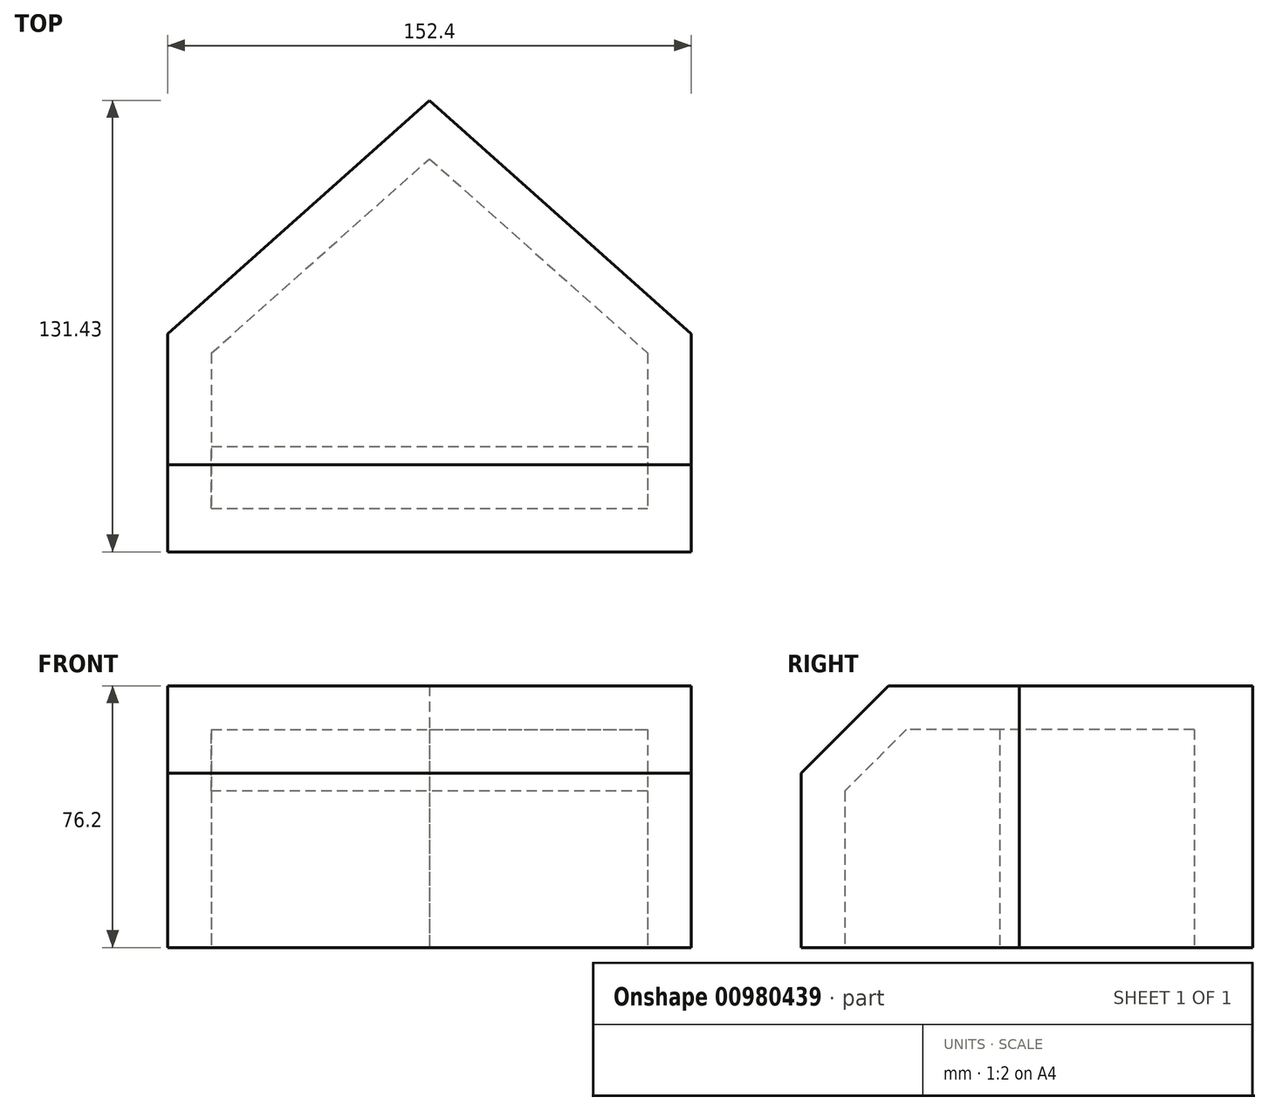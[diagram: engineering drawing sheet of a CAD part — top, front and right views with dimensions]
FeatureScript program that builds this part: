
annotation { "Feature Type Name" : "Feature", "Feature Type Description" : "" }
export const myFeature = defineFeature(function(context is Context, id is Id, definition is map)
    precondition{}
    {
        {
            var Q0;
            Q0=qCreatedBy(makeId("Top.planeOp"),FACE);
            var sketch = newSketch(context, id + "F0", { "sketchPlane" : qUnion([Q0])});
            skLineSegment(sketch, "E0.bottom", {"start": v(-76.2, 17.86) * mm, "end": v(76.2, 17.86) * mm});
            skLineSegment(sketch, "E0.top", {"start": v(-76.2, -45.64) * mm, "end": v(76.2, -45.64) * mm});
            skLineSegment(sketch, "E0.left", {"start": v(-76.2, 17.86) * mm, "end": v(-76.2, -45.64) * mm});
            skLineSegment(sketch, "E0.right", {"start": v(76.2, 17.86) * mm, "end": v(76.2, -45.64) * mm});
            skPoint(sketch, "E1", {"position": v(0, 17.86) * mm});
            skLineSegment(sketch, "E2", {"start": v(0, 17.86) * mm, "end": v(0, 117.38) * mm, "construction": true});
            skLineSegment(sketch, "E3", {"start": v(-76.2, 17.86) * mm, "end": v(0, 85.8) * mm});
            skLineSegment(sketch, "E4", {"start": v(0, 85.8) * mm, "end": v(76.2, 17.86) * mm});
            skSolve(sketch);
        }
        {
            var Q0;
            Q0=makeQuery(id+"F0.imprint","IMPRINT",FACE,{"disambiguationData":[TD([[makeQuery(id+"F0.imprint","IMPRINT",EDGE,{"derivedFrom":sQuery(id+"F0.wireOp",EDGE,"E0.bottom")}),-1.0]])]});
            var Q1;
            Q1=makeQuery(id+"F0.imprint","IMPRINT",FACE,{"disambiguationData":[TD([[makeQuery(id+"F0.imprint","IMPRINT",EDGE,{"derivedFrom":sQuery(id+"F0.wireOp",EDGE,"E0.bottom")}),1.0]])]});
            extrude(context, id + "F1", {"entities" : qUnion([Q0, Q1]), "depth" : 76.2 * mm, "offsetDistance" : 25.4 * mm});
        }
        {
            var Q0;
            Q0=makeQuery(id+"F1.opExtrude","CAP_EDGE",EDGE,{"disambiguationData":[OSD([sQuery(id+"F0.wireOp",EDGE,"E0.top")])],"isStart":false});
            chamfer(context, id + "F2", {"entities" : qUnion([Q0]), "width" : 25.4 * mm, "tangentPropagation" : true});
        }
        {
            var Q0;
            Q0=makeQuery(id+"F1.opExtrude","CAP_FACE",FACE,{"disambiguationData":[OSD([sQuery(id+"F0.wireOp",EDGE,"E0.top"),sQuery(id+"F0.wireOp",EDGE,"E0.left"),sQuery(id+"F0.wireOp",EDGE,"E0.right"),sQuery(id+"F0.wireOp",EDGE,"E3"),sQuery(id+"F0.wireOp",EDGE,"E4")])],"isStart":true});
            shell(context, id + "F3", {"entities" : qUnion([Q0]), "thickness" : 12.7 * mm});
        }
    });
